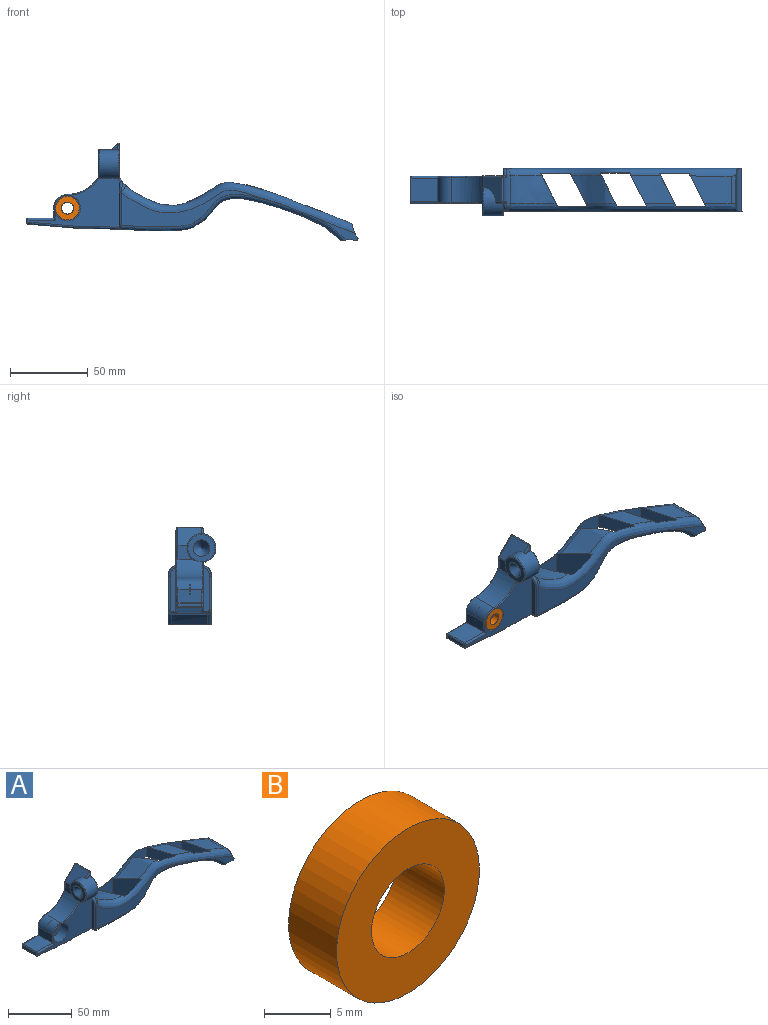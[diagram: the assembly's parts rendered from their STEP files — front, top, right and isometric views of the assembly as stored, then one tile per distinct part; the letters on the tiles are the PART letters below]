
ASSEMBLY  parts=2 mates=1
PART A: 117 faces, bbox 239.4x32.9x66.3 mm
  f0: plane 59.23x31.47mm, normal (0,-1,0), area 836.1mm2, adj f3,f16,f67,f78,f86,f87,f88,f89
  f1: plane 2.16x2.15mm, normal (0,-1,0), area 2.3mm2, adj f76,f77,f111
  f2: cylinder r=1.27mm len=11.14mm, axis (0,0,-1), area 18.7mm2, adj f26,f35,f85,f92,f105,f106
  f3: cylinder r=1.27mm len=10.93mm, axis (0,0,1), area 14.5mm2, adj f0,f4,f26,f88,f110
  f4: bspline ~2.5x1.43mm, area 1.5mm2, adj f3,f34,f90,f91,f110
  f5: plane 103.36x23.76mm, normal (0,1,0), area 714mm2, adj f48,f57,f58,f59,f60,f61,f70
  f6: plane 103.37x23.76mm, normal (0,-1,0), area 714mm2, adj f50,f52,f53,f54,f55,f56,f64
  f7: extruded ~26.08x17.7mm, area 412.5mm2, adj f22,f38,f48,f50
  f8: extruded ~28.04x17.7mm, area 357.1mm2, adj f36,f42,f48,f50
  f9: extruded ~28.04x17.7mm, area 375.9mm2, adj f40,f47,f48,f50
  f10: extruded ~21.25x14.46mm, area 62.9mm2, adj f11,f17,f45,f46,f55
  f11: extruded ~3.73x2.19mm, area 2.7mm2, adj f10,f13,f46,f56
  f12: extruded ~20.01x3.73mm, area 70.7mm2, adj f13,f18,f47,f61
  f13: extruded ~48.38x22.78mm, area 832.3mm2, adj f11,f12,f19,f36,f39,f40,f41,f42
  f14: plane 28.01x3.84mm, normal (-1,0,0), area 102.6mm2, adj f35,f68,f69,f70,f71,f72,f73,f83
  f15: cylinder r=12.23mm len=17.7mm, axis (0,1,0), area 135.5mm2, adj f23,f30,f49,f51,f67,f73,f78,f82
  f16: plane 28.01x3.84mm, normal (-1,0,0), area 102.6mm2, adj f0,f62,f63,f64,f65,f66,f67,f86
  f17: extruded ~27.93x22.78mm, area 612.6mm2, adj f10,f18,f29,f44,f45,f53,f58,f62
  f18: extruded ~21.25x12.66mm, area 55mm2, adj f12,f17,f44,f47,f60
  f19: extruded ~41.11x22.78mm, area 633.1mm2, adj f13,f20,f36,f37,f38,f39,f52,f57
  f20: cylinder r=18.72mm len=27.86mm, axis (0,1,0), area 256.6mm2, adj f19,f24,f25,f52,f57,f75
  f21: cylinder r=18.72mm len=27.86mm, axis (0,1,0), area 228.9mm2, adj f24,f25,f48,f50,f74,f75
  f22: plane 17.84x2.64mm, normal (0.38,0,0.93), area 50.1mm2, adj f7,f48,f50,f74
  f23: extruded ~29.53x17.7mm, area 497.4mm2, adj f15,f45,f48,f50
  f24: plane 27.36x14.83mm, normal (0,-1,0), area 83.3mm2, adj f20,f21,f50,f52,f75
  f25: plane 27.36x14.83mm, normal (0,1,0), area 83.3mm2, adj f20,f21,f48,f57,f75
  f26: plane 15.1x7.85mm, normal (-1,0,0), area 118.5mm2, adj f2,f3,f27,f91
  f27: plane 17.27x15.1mm, normal (0,0,1), area 260.8mm2, adj f26,f85,f88,f102
  f28: plane 15.1x2.46mm, normal (-1,0,0), area 37.2mm2, adj f84,f87,f99,f102
  f29: extruded ~59.38x15.1mm, area 898.6mm2, adj f17,f83,f86,f99
  f30: plane 23.77x21.54mm, normal (1,0,0), area 417.8mm2, adj f15,f77,f78,f81,f96,f115
  f31: plane 15.1x11.74mm, normal (-0.71,0,0.7), area 175.2mm2, adj f32,f76,f80,f96,f111
  f32: plane 8.97x8.62mm, normal (-1,0,0), area 56.9mm2, adj f31,f33,f79,f111
  f33: cylinder r=23.23mm len=20.73mm, axis (0,1,0), area 405mm2, adj f32,f34,f79,f89,f94,f111,f112,f116
  f34: cylinder r=8.86mm len=16.37mm, axis (0,1,0), area 201.1mm2, adj f4,f33,f90,f91,f92,f93
  f35: plane 59.22x51.93mm, normal (0,1,0), area 1133.3mm2, adj f2,f14,f73,f79,f80,f81,f82,f83
  f36: plane 21.68x11.76mm, normal (0.89,0.45,0), area 193.5mm2, adj f8,f13,f19,f37,f39,f48,f50
  f37: plane 19.42x16.17mm, normal (0,1,0), area 146.1mm2, adj f19,f36,f38,f50
  f38: plane 21.59x13.04mm, normal (-0.89,-0.45,0), area 198.6mm2, adj f7,f19,f37,f39,f48,f50
  f39: plane 19.13x14.69mm, normal (0,-1,0), area 143.9mm2, adj f13,f19,f36,f38,f48
  f40: plane 22.78x16.89mm, normal (0.89,0.45,0), area 274.8mm2, adj f9,f13,f41,f43,f48,f50
  f41: plane 19.14x12.92mm, normal (0,1,0), area 170.6mm2, adj f13,f40,f42,f50
  f42: plane 21.91x11.97mm, normal (-0.89,-0.45,0), area 215.5mm2, adj f8,f13,f41,f43,f48,f50
  f43: plane 19.55x15.5mm, normal (0,-1,0), area 197.4mm2, adj f13,f40,f42,f48
  f44: plane 19.24x17.97mm, normal (0,-1,0), area 312.9mm2, adj f17,f18,f45,f47,f48
  f45: plane 21.97x18mm, normal (0.89,0.45,0), area 403.9mm2, adj f10,f17,f23,f44,f46,f48,f50
  f46: plane 22.83x19.16mm, normal (0,1,0), area 318.7mm2, adj f10,f11,f13,f45,f47,f50
  f47: plane 22.25x21.75mm, normal (-0.89,-0.45,0), area 417.3mm2, adj f9,f12,f13,f18,f44,f46,f48,f50
  f48: bspline ~158.15x35.39mm, area 1143mm2, adj f5,f7,f8,f9,f21,f22,f23,f25
  f49: torus R=17.31mm, axis (0,-1,0), area 13.2mm2, adj f15,f48,f72
  f50: bspline ~157.94x35.39mm, area 1141.4mm2, adj f6,f7,f8,f9,f21,f22,f23,f24
  f51: torus R=17.31mm, axis (0,-1,0), area 13.2mm2, adj f15,f50,f66
  f52: bspline ~44.08x25.33mm, area 193mm2, adj f6,f19,f20,f24,f50,f54
  f53: bspline ~28.6x3.66mm, area 106.5mm2, adj f6,f17,f55,f63
  f54: bspline ~53.52x17.85mm, area 222.8mm2, adj f6,f13,f52,f56
  f55: bspline ~24.07x5.84mm, area 85.3mm2, adj f6,f10,f53,f56
  f56: bspline ~21.72x14.17mm, area 17.2mm2, adj f6,f11,f54,f55
  f57: bspline ~44.08x25.33mm, area 193mm2, adj f5,f19,f20,f25,f48,f59
  f58: bspline ~28.6x3.66mm, area 106.5mm2, adj f5,f17,f60,f69
  f59: bspline ~53.52x17.85mm, area 222.8mm2, adj f5,f13,f57,f61
  f60: bspline ~24.07x5.84mm, area 85.3mm2, adj f5,f18,f58,f61
  f61: bspline ~20.75x13.6mm, area 17.2mm2, adj f5,f12,f59,f60
  f62: cylinder r=1.27mm len=3.77mm, axis (0,1,0), area 6.2mm2, adj f16,f17,f63,f86
  f63: bspline ~3.11x3.11mm, area 6.4mm2, adj f16,f53,f62,f64
  f64: cylinder r=1.27mm len=21.39mm, axis (0,0,1), area 42.7mm2, adj f6,f16,f63,f65
  f65: bspline ~1.29x1.29mm, area 0.1mm2, adj f16,f50,f64,f66
  f66: bspline ~9.42x6.73mm, area 22.6mm2, adj f16,f51,f65,f67
  f67: cylinder r=1.27mm len=2.27mm, axis (0,1,0), area 1mm2, adj f0,f15,f16,f66,f78
  f68: cylinder r=1.27mm len=3.77mm, axis (0,1,0), area 6.2mm2, adj f14,f17,f69,f83
  f69: bspline ~3.11x3.11mm, area 6.4mm2, adj f14,f58,f68,f70
  f70: cylinder r=1.27mm len=21.39mm, axis (0,0,-1), area 42.7mm2, adj f5,f14,f69,f71
  f71: bspline ~1.29x1.29mm, area 0.1mm2, adj f14,f48,f70,f72
  f72: bspline ~9.42x6.73mm, area 22.6mm2, adj f14,f49,f71,f73
  f73: cylinder r=1.27mm len=2.27mm, axis (0,1,0), area 1mm2, adj f14,f15,f35,f72,f82
  f74: cylinder r=1.27mm len=22.51mm, axis (0,1,0), area 26.1mm2, adj f21,f22,f48,f50
  f75: cylinder r=1.27mm len=27.86mm, axis (0,1,0), area 85.8mm2, adj f20,f21,f24,f25
  f76: cylinder r=1.27mm len=4.96mm, axis (0.7,0,0.71), area 8.7mm2, adj f1,f31,f97,f111
  f77: cylinder r=1.27mm len=4.25mm, axis (0,0,-1), area 6.2mm2, adj f1,f30,f97,f111,f115
  f78: torus R=13.5mm, axis (0,-1,0), area 7.1mm2, adj f0,f15,f30,f67,f111,f115
  f79: cylinder r=1.27mm len=8.62mm, axis (0,0,-1), area 15.6mm2, adj f32,f33,f35,f80,f94
  f80: cylinder r=1.27mm len=12.64mm, axis (-0.7,0,-0.71), area 31mm2, adj f31,f35,f79,f95
  f81: cylinder r=1.27mm len=20.06mm, axis (0,0,1), area 38.3mm2, adj f30,f35,f82,f95
  f82: torus R=13.5mm, axis (0,-1,0), area 9.6mm2, adj f15,f35,f73,f81
  f83: bspline ~141.69x8.53mm, area 119mm2, adj f14,f17,f29,f35,f68,f98
  f84: cylinder r=1.27mm len=2.46mm, axis (0,0,-1), area 3.7mm2, adj f28,f35,f98,f101
  f85: cylinder r=1.27mm len=18.54mm, axis (-1,0,0), area 35.1mm2, adj f2,f27,f35,f101
  f86: bspline ~85.46x6.81mm, area 119mm2, adj f0,f16,f17,f29,f62,f100
  f87: cylinder r=1.27mm len=2.46mm, axis (0,0,1), area 3.7mm2, adj f0,f28,f100,f103
  f88: cylinder r=1.27mm len=18.54mm, axis (1,0,0), area 35.1mm2, adj f0,f3,f27,f103
  f89: torus R=23.87mm, axis (0,-1,0), area 23.6mm2, adj f0,f33,f90,f110,f112,f116
  f90: torus R=8.23mm, axis (0,-1,0), area 9mm2, adj f4,f34,f89,f110
  f91: cylinder r=0.64mm len=15.1mm, axis (0,1,0), area 1.7mm2, adj f4,f26,f34,f92
  f92: bspline ~2.62x1.52mm, area 1.5mm2, adj f2,f34,f91,f93
  f93: torus R=8.23mm, axis (0,-1,0), area 9.8mm2, adj f34,f35,f92,f94
  f94: torus R=23.87mm, axis (0,-1,0), area 26.4mm2, adj f33,f35,f79,f93
  f95: bspline ~3.08x1.88mm, area 1.6mm2, adj f80,f81,f96
  f96: cylinder r=0.64mm len=15.1mm, axis (0,1,0), area 22.6mm2, adj f30,f31,f95,f97
  f97: bspline ~3.08x1.88mm, area 1.6mm2, adj f76,f77,f96
  f98: bspline ~1.47x1.27mm, area 0.9mm2, adj f83,f84,f99
  f99: cylinder r=0.64mm len=15.1mm, axis (0,1,0), area 14.1mm2, adj f28,f29,f98,f100
  f100: bspline ~1.47x1.27mm, area 0.9mm2, adj f86,f87,f99
  f101: bspline ~1.52x1.27mm, area 0.9mm2, adj f84,f85,f102
  f102: cylinder r=0.64mm len=15.1mm, axis (0,1,0), area 15.1mm2, adj f27,f28,f101,f103
  f103: bspline ~1.52x1.27mm, area 0.9mm2, adj f87,f88,f102
  f104: cylinder r=4.92mm len=9.84mm, axis (0,-1,0), area 7.3mm2, adj f35,f105
  f105: plane 16.62x16.52mm, normal (0,-1,0), area 140.8mm2, adj f2,f104,f106
  f106: cylinder r=8.31mm len=16.62mm, axis (0,-1,0), area 448.4mm2, adj f2,f105,f107
  f107: plane 16.62x16.62mm, normal (0,1,0), area 141mm2, adj f106,f108
  f108: cylinder r=4.92mm len=9.84mm, axis (0,-1,0), area 7.3mm2, adj f107,f109
  f109: plane 16.62x16.62mm, normal (0,-1,0), area 141mm2, adj f108,f110
  f110: cylinder r=8.31mm len=16.62mm, axis (0,-1,0), area 447.1mm2, adj f0,f3,f4,f89,f90,f109
  f111: cylinder r=9.3mm len=18.61mm, axis (1,0,0), area 401.9mm2, adj f0,f1,f31,f32,f33,f76,f77,f78
  f112: plane 17.45x17.38mm, normal (-1,0,0), area 147.7mm2, adj f33,f89,f113,f116
  f113: cone r=5.28mm half-angle=40deg, axis (-1,0,0), area 136mm2, adj f112,f114
  f114: plane 0.28x0.28mm, normal (-1,0,0), area 0.1mm2, adj f113
  f115: torus R=8.67mm, axis (1,0,0), area 26.8mm2, adj f30,f77,f78,f111
  f116: torus R=8.67mm, axis (1,0,0), area 51.2mm2, adj f0,f33,f89,f111,f112
PART B: 4 faces, bbox 15.2x5.1x15.2 mm
  f0: cylinder r=7.58mm len=15.15mm, axis (0,-1,0), area 241.8mm2, adj f1,f2
  f1: plane 15.15x15.15mm, normal (0,1,0), area 133.5mm2, adj f0,f3
  f2: plane 15.15x15.15mm, normal (0,-1,0), area 133.5mm2, adj f0,f3
  f3: cylinder r=3.86mm len=7.72mm, axis (0,-1,0), area 123.2mm2, adj f1,f2
PLACE A rot(axis=(-0.32,-0.18,0.93),0deg) t=(-13.7,-26.49,-63.05)mm
PLACE B rot(axis=(-0.32,-0.18,0.93),0deg) t=(-13.7,-26.43,-63.05)mm
MATE slider A.f34 <-> B.f0  axis (0,-1,0) through (-107.47,-35.31,-30.08)mm
